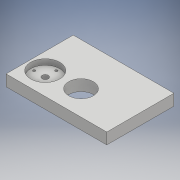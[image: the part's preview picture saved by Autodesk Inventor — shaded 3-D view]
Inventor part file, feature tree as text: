
AUTODESK INVENTOR PART (.ipt)
format: ipt  version: 2017 SP1 (Build 210196100, 196)  size: 137,728 bytes
history: native  units: mm
features: extrude x4, sketch x4
ambient origin geometry x8: Origin, YZ Plane, XZ Plane, XY Plane, X Axis, Y Axis, Z Axis, Center Point
bodies: Solide1 (feature_tree)
feature tree (8):
  extrude  "Extrusion1"  Depth=90.0mm
  extrude  "Extrusion2"  Depth=60.0mm
  extrude  "Extrusion3"  Depth=10.0mm TaperAngle=0.0deg
  extrude  "Extrusion4"  Depth=26.0mm
  sketch  "Esquisse1"
  sketch  "Esquisse2"
  sketch  "Esquisse3"
  sketch  "Esquisse4"
